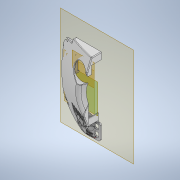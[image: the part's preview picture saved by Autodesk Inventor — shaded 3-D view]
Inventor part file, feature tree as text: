
AUTODESK INVENTOR PART (.ipt)
format: ipt  version: 2022 (Build 260153000, 153)  size: 4,329,472 bytes
history: native  units: mm
features: reference x66, fillet x33, sketch x31, extrude x26, other x24, projected_geometry x19, revolve x6, chamfer x1
ambient origin geometry x8: Origin, YZ Plane, XZ Plane, XY Plane, X Axis, Y Axis, Z Axis, Center Point
bodies: Body1 (feature_tree)
feature tree (206):
  other  "Твердое тело1"
  revolve  "Вращение1"
  other  "РабПлоскость1"
  extrude  "Выдавливание1"  Depth=4.363323mm
  extrude  "Выдавливание2"  Depth=7.8mm
  other  "РабПлоскость2"
  revolve  "Вращение2"
  revolve  "Вращение3"
  other  "РабПлоскость3"
  extrude  "Выдавливание4"  Depth=1.0mm
  fillet  "Сопряжение3"  Radius=1.5mm
  extrude  "Выдавливание6"  TaperAngle=90.0deg  [1 undecoded]
  fillet  "Сопряжение4"  Radius=90.0mm
  extrude  "Выдавливание7"  Depth=200.0mm TaperAngle=0.0deg
  extrude  "Выдавливание8"  Depth=1.0mm
  extrude  "Выдавливание9"  Depth=1.0mm
  extrude  "Выдавливание10"  TaperAngle=90.0deg  [1 undecoded]
  fillet  "Сопряжение5"  Radius=2.0mm
  revolve  "Вращение4"
  extrude  "Выдавливание11"  Depth=2.0mm
  extrude  "Выдавливание12"  Depth=0.5mm
  fillet  "Сопряжение12"  [1 undecoded]
  extrude  "Выдавливание14"  Depth=0.5mm
  extrude  "Выдавливание15"  Depth=90.0mm TaperAngle=0.0deg
  extrude  "Выдавливание16"  Depth=0.8mm
  revolve  "Вращение5"
  fillet  "Сопряжение14"  Radius=5.0mm
  fillet  "Сопряжение15"  Radius=1.5mm
  fillet  "Сопряжение16"  Radius=90.0mm
  fillet  "Сопряжение17"  Radius=1.0mm
  fillet  "Сопряжение18"  Radius=4.0mm
  fillet  "Сопряжение19"  Radius=4.0mm
  fillet  "Сопряжение20"  Radius=3.0mm
  fillet  "Сопряжение21"  Radius=3.0mm
  fillet  "Сопряжение22"  Radius=2.0mm
  fillet  "Сопряжение23"  Radius=6.0mm
  fillet  "Сопряжение24"  Radius=30.0mm
  fillet  "Сопряжение25"  Radius=1.5mm
  fillet  "Сопряжение26"  Radius=30.0mm
  sketch  "Эскиз25"
  other  "РабПлоскость5"
  extrude  "Выдавливание18"  Depth=0.5mm
  extrude  "Выдавливание19"  Depth=0.5mm
  extrude  "Выдавливание20"  Depth=0.5mm
  fillet  "Сопряжение27"  Radius=0.5mm
  revolve  "Вращение6"
  extrude  "Выдавливание21"  Depth=2.0mm TaperAngle=0.0deg
  fillet  "Сопряжение28"  Radius=5.0mm
  fillet  "Сопряжение29"  Radius=5.0mm
  extrude  "Выдавливание22"  TaperAngle=90.0deg  [1 undecoded]
  extrude  "Выдавливание23"  Depth=1.0mm TaperAngle=0.0deg
  fillet  "Сопряжение30"  Radius=1.5mm
  other  "РабПлоскость6"
  extrude  "Выдавливание24"  Depth=1.0mm TaperAngle=0.0deg
  extrude  "Выдавливание25"  Depth=2.0mm
  fillet  "Сопряжение32"  Radius=1.5mm
  other  "РабПлоскость7"
  extrude  "Выдавливание26"  Depth=3.0mm
  extrude  "Выдавливание27"  Depth=3.0mm
  fillet  "Сопряжение33"  Radius=1.5mm
  fillet  "Сопряжение34"  Radius=2.0mm
  fillet  "Сопряжение35"  Radius=1.0mm
  fillet  "Сопряжение36"  Radius=1.0mm
  fillet  "Сопряжение37"  Radius=2.0mm
  fillet  "Сопряжение38"  Radius=10.0mm
  fillet  "Сопряжение39"  Radius=1.0mm
  fillet  "Сопряжение40"  [1 undecoded]
  fillet  "Сопряжение41"  Radius=1.7mm
  chamfer  "Фаска1"  Distance=3.0mm
  other  "РабПлоскость8"
  extrude  "Выдавливание28"  Depth=2.0mm
  other  "РабПлоскость9"
  extrude  "Выдавливание29"  Depth=2.0mm
  fillet  "Сопряжение42"  Radius=1.0mm
  fillet  "Сопряжение43"  Radius=3.0mm
  other  "РабПлоскость10"
  extrude  "Выдавливание30"  Depth=2.0mm
  reference  "Ссылка1"
  sketch  "Эскиз2"
  reference  "Ссылка2"
  reference  "Ссылка3"
  projected_geometry  "Спроецированная петля1"
  sketch  "Эскиз3"
  reference  "Ссылка4"
  reference  "Ссылка5"
  reference  "Ссылка6"
  reference  "Ссылка7"
  reference  "Ссылка8"
  sketch  "Эскиз5"
  reference  "Ссылка14"
  reference  "Ссылка16"
  sketch  "Эскиз6"
  reference  "Ссылка17"
  sketch  "Эскиз7"
  reference  "Ссылка18"
  sketch  "Эскиз9"
  reference  "Ссылка20"
  reference  "Ссылка21"
  sketch  "Эскиз10"
  reference  "Ссылка22"
  reference  "Ссылка23"
  reference  "Ссылка24"
  reference  "Ссылка25"
  reference  "Ссылка27"
  reference  "Ссылка28"
  reference  "Ссылка29"
  reference  "Ссылка30"
  reference  "Ссылка31"
  reference  "Ссылка32"
  reference  "Ссылка33"
  reference  "Ссылка34"
  reference  "Ссылка35"
  reference  "Ссылка36"
  reference  "Ссылка37"
  reference  "Ссылка38"
  reference  "Ссылка39"
  reference  "Ссылка40"
  reference  "Ссылка41"
  reference  "Ссылка42"
  sketch  "Эскиз11"
  projected_geometry  "Спроецированная петля2"
  sketch  "Эскиз12"
  projected_geometry  "Спроецированная петля3"
  reference  "Ссылка45"
  reference  "Ссылка46"
  reference  "Ссылка47"
  reference  "Ссылка48"
  reference  "Ссылка49"
  reference  "Ссылка50"
  reference  "Ссылка51"
  reference  "Ссылка52"
  reference  "Ссылка53"
  reference  "Ссылка54"
  sketch  "Эскиз13"
  projected_geometry  "Спроецированная петля4"
  sketch  "Эскиз14"
  sketch  "Эскиз15"
  sketch  "Эскиз16"
  projected_geometry  "Спроецированная петля5"
  reference  "Ссылка55"
  reference  "Ссылка56"
  reference  "Ссылка57"
  sketch  "Эскиз20"
  reference  "Ссылка66"
  reference  "Ссылка67"
  reference  "Ссылка68"
  reference  "Ссылка69"
  reference  "Ссылка70"
  sketch  "Эскиз21"
  reference  "Ссылка71"
  reference  "Ссылка72"
  sketch  "Эскиз22"
  projected_geometry  "Спроецированная петля9"
  projected_geometry  "Спроецированная петля10"
  projected_geometry  "Спроецированная петля11"
  projected_geometry  "Спроецированная петля12"
  reference  "Ссылка73"
  reference  "Ссылка74"
  sketch  "Эскиз24"
  reference  "Ссылка75"
  sketch  "Эскиз26"
  projected_geometry  "Спроецированная петля14"
  sketch  "Эскиз27"
  reference  "Ссылка76"
  sketch  "Эскиз28"
  sketch  "Эскиз29"
  reference  "Ссылка77"
  sketch  "Эскиз30"
  projected_geometry  "Спроецированная петля15"
  projected_geometry  "Спроецированная петля16"
  sketch  "Эскиз31"
  reference  "Ссылка78"
  sketch  "Эскиз32"
  reference  "Ссылка79"
  projected_geometry  "Спроецированная петля17"
  projected_geometry  "Спроецированная петля18"
  sketch  "Эскиз33"
  projected_geometry  "Спроецированная петля19"
  sketch  "Эскиз34"
  projected_geometry  "Спроецированная петля20"
  reference  "Ссылка80"
  projected_geometry  "Спроецированная петля21"
  sketch  "Эскиз35"
  projected_geometry  "Спроецированная петля22"
  reference  "Ссылка81"
  projected_geometry  "Спроецированная петля23"
  sketch  "Эскиз36"
  reference  "Ссылка82"
  sketch  "Эскиз37"
  reference  "Ссылка83"
  sketch  "Эскиз38"
  reference  "Ссылка84"
  other  "<userpath>\Documents\Git\MZCAT_2024_construction\MZCAT_2024_RPI_2\MZCAT_4.iam"
  other  "MZCAT_4.iam"
  other  "LD19:1"
  other  "commutationCATboard:1"
  other  "lidar_shatun:1"
  other  "diffuser:1"
  other  "lidar_krestovina_base:1"
  other  "lidar_krestovina:1"
  other  "heatsink_40x40x11mm_blk:1"
  other  "<userpath>\Documents\Git\MZCAT_2024\MZCAT_4.iam"
  other  "30mm Fan Mockup 3010 v5:1"
  other  "MZCAT_motherboard_fnl:1"
  other  "motherboard_plate:1"
  other  "bonnet_fixator:1"
note: 5 required parameter values undecoded (feature->parameter linkage not recoverable at this tier; creation-order binding heuristic only, values carry confidence <= 0.55)
